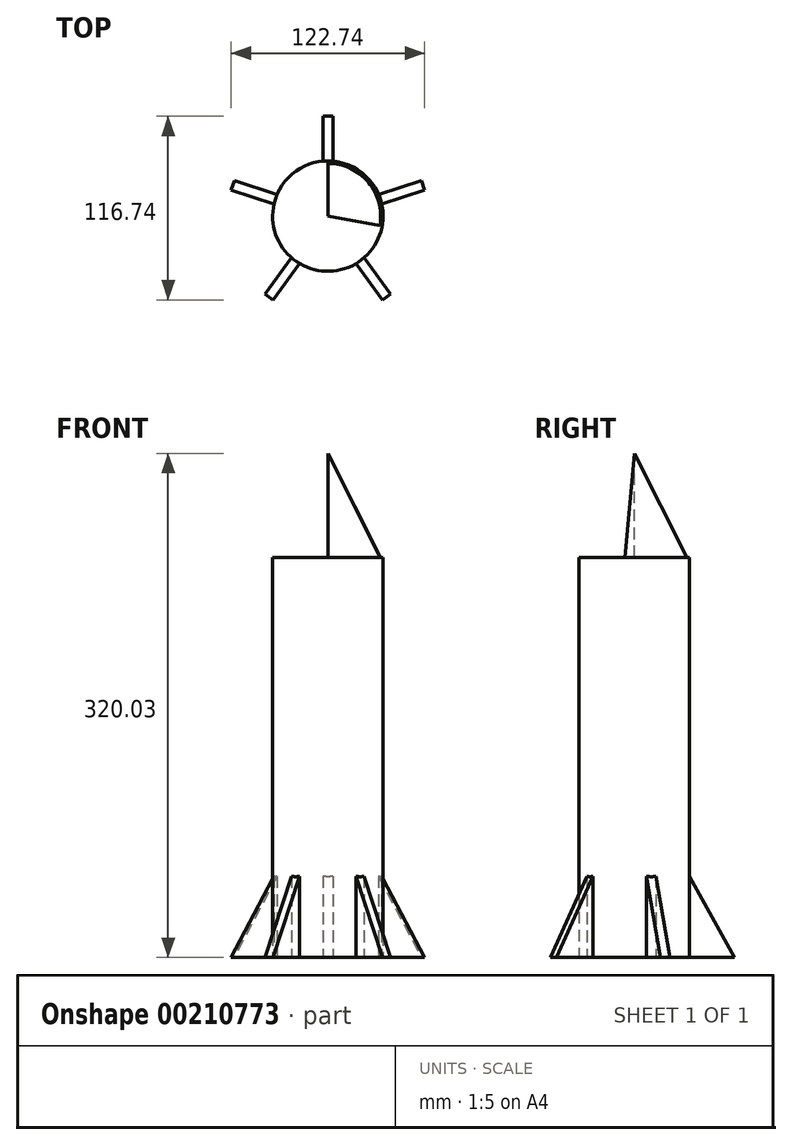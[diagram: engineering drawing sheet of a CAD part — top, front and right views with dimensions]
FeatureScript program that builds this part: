
annotation { "Feature Type Name" : "Feature", "Feature Type Description" : "" }
export const myFeature = defineFeature(function(context is Context, id is Id, definition is map)
    precondition{}
    {
        {
            var Q0;
            Q0=qCreatedBy(makeId("Top.planeOp"),FACE);
            var sketch = newSketch(context, id + "F0", { "sketchPlane" : qUnion([Q0])});
            skCircle(sketch, "E0", {"center": v(0, 0) * mm, "radius": 35.05 * mm});
            skSolve(sketch);
        }
        {
            var Q0;
            Q0=qSketchRegion(id+"F0",true);
            extrude(context, id + "F1", {"entities" : qUnion([Q0]), "depth" : 254 * mm});
        }
        {
            var Q0;
            Q0=qCreatedBy(makeId("Right.planeOp"),FACE);
            var sketch = newSketch(context, id + "F2", { "sketchPlane" : qUnion([Q0])});
            skLineSegment(sketch, "E1", {"start": v(0, 0) * mm, "end": v(0, 114.3) * mm});
            skLineSegment(sketch, "E2", {"start": v(0, 114.3) * mm, "end": v(63.5, 0) * mm});
            skLineSegment(sketch, "E3", {"start": v(63.5, 0) * mm, "end": v(0, 0) * mm});
            skSolve(sketch);
        }
        {
            var Q0;
            Q0=qSketchRegion(id+"F2",true);
            extrude(context, id + "F3", {"entities" : qUnion([Q0]), "operationType" : NewBodyOperationType.ADD, "endBound" : BoundingType.SYMMETRIC, "depth" : 6.35 * mm});
        }
        {
            var Q0;
            Q0=makeQuery(id+"F1.opExtrude","SWEPT_BODY",BODY,{"disambiguationData":[OSD([sQuery(id+"F0.wireOp",EDGE,"E0")])]});
            var Q1;
            Q1=makeQuery(id+"F1.opExtrude","SWEPT_FACE",FACE,{"disambiguationData":[OSD([sQuery(id+"F0.wireOp",EDGE,"E0")])]});
            circularPattern(context, id + "F4", {"entities" : qUnion([Q0]), "axis" : qUnion([Q1]), "angle" : 360 * degree, "instanceCount" : 5, "equalSpace" : true});
        }
        {
            var Q0;
            Q0=qCreatedBy(makeId("Right.planeOp"),FACE);
            var sketch = newSketch(context, id + "F5", { "sketchPlane" : qUnion([Q0])});
            skLineSegment(sketch, "E4", {"start": v(0, 253.77) * mm, "end": v(0, 320.03) * mm});
            skLineSegment(sketch, "E5", {"start": v(0, 320.03) * mm, "end": v(34.45, 252.27) * mm});
            skLineSegment(sketch, "E6", {"start": v(34.45, 252.27) * mm, "end": v(0, 253.77) * mm});
            skSolve(sketch);
        }
        {
            var Q0;
            Q0=makeQuery(id+"F5.imprint","IMPRINT",FACE,{"disambiguationData":[TD([[makeQuery(id+"F5.imprint","IMPRINT",EDGE,{"derivedFrom":sQuery(id+"F5.wireOp",EDGE,"E4")}),-1.0]])]});
            var Q1;
            Q1=sQuery(id+"F5.wireOp",EDGE,"E4");
            revolve(context, id + "F6", {"operationType" : NewBodyOperationType.ADD, "entities" : qUnion([Q0]), "axis" : qUnion([Q1]), "revolveType" : RevolveType.ONE_DIRECTION, "oppositeDirection" : true, "angle" : 100 * degree});
        }
    });
